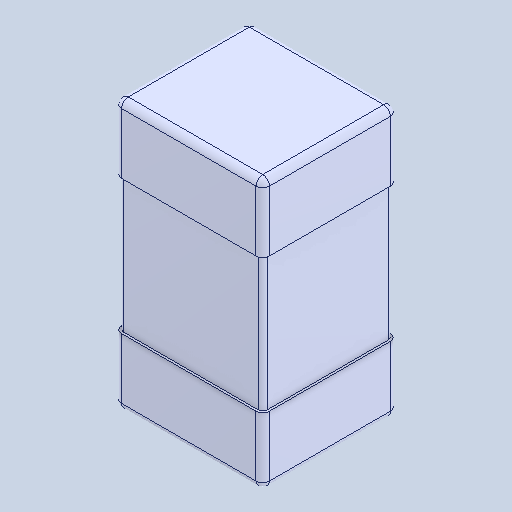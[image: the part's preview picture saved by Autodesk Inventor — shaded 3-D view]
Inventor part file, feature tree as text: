
AUTODESK INVENTOR PART (.ipt)
format: ipt  version: 2025 (Build 290162000, 162)  size: 125,952 bytes
history: native  units: mm
features: fillet x1, mirror x1, other x1
ambient origin geometry x8: Origin, YZ Plane, XZ Plane, XY Plane, X Axis, Y Axis, Z Axis, Center Point
bodies: Solid1 (feature_tree), Solid2 (feature_tree), Solid3 (feature_tree)
feature tree (3):
  fillet  "Fillet1"  [1 undecoded]
  mirror  "Mirror2"
  other  "Boss-Extrude2"
note: 1 required parameter value undecoded (feature->parameter linkage not recoverable at this tier; creation-order binding heuristic only, values carry confidence <= 0.55)
